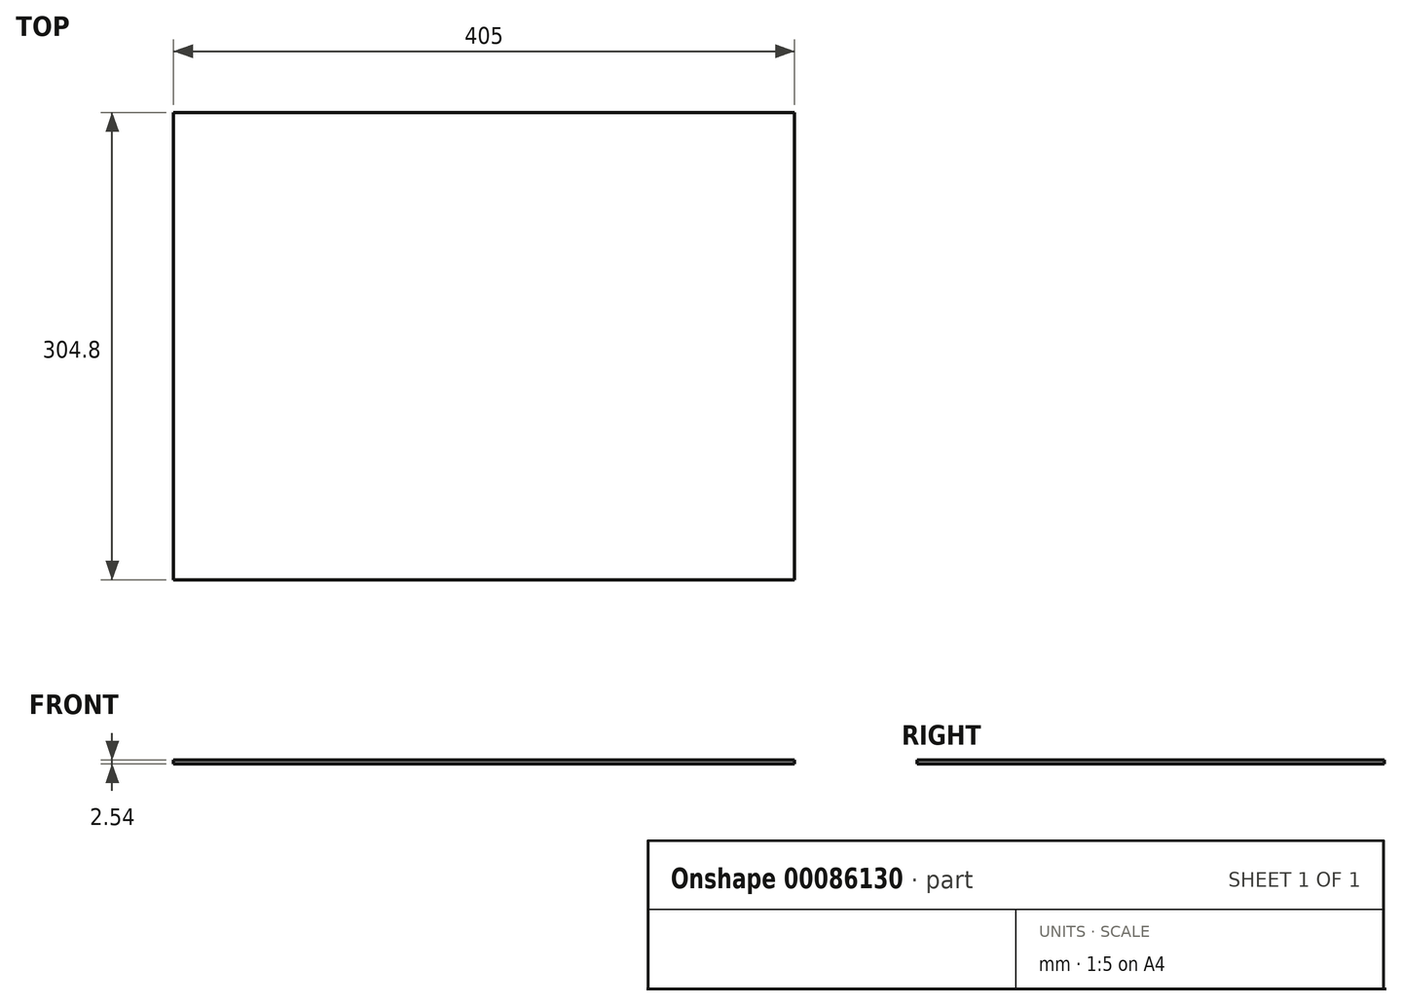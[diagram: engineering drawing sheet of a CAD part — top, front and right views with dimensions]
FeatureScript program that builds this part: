
annotation { "Feature Type Name" : "Feature", "Feature Type Description" : "" }
export const myFeature = defineFeature(function(context is Context, id is Id, definition is map)
    precondition{}
    {
        {
            var Q0;
            Q0=qCreatedBy(makeId("Top.planeOp"),FACE);
            var sketch = newSketch(context, id + "F0", { "sketchPlane" : qUnion([Q0])});
            skLineSegment(sketch, "E0.bottom", {"start": v(202.5, 152.4) * mm, "end": v(-202.5, 152.4) * mm});
            skLineSegment(sketch, "E0.top", {"start": v(202.5, -152.4) * mm, "end": v(-202.5, -152.4) * mm});
            skLineSegment(sketch, "E0.left", {"start": v(202.5, 152.4) * mm, "end": v(202.5, -152.4) * mm});
            skLineSegment(sketch, "E0.right", {"start": v(-202.5, 152.4) * mm, "end": v(-202.5, -152.4) * mm});
            skPoint(sketch, "E0.middle", {"position": v(0, 0) * mm});
            skSolve(sketch);
        }
        {
            var Q0;
            Q0=makeQuery(id+"F0.imprint","IMPRINT",FACE,{"disambiguationData":[TD([[makeQuery(id+"F0.imprint","IMPRINT",EDGE,{"derivedFrom":sQuery(id+"F0.wireOp",EDGE,"E0.bottom")}),1.0]])]});
            extrude(context, id + "F1", {"entities" : qUnion([Q0]), "depth" : 2.54 * mm});
        }
    });
